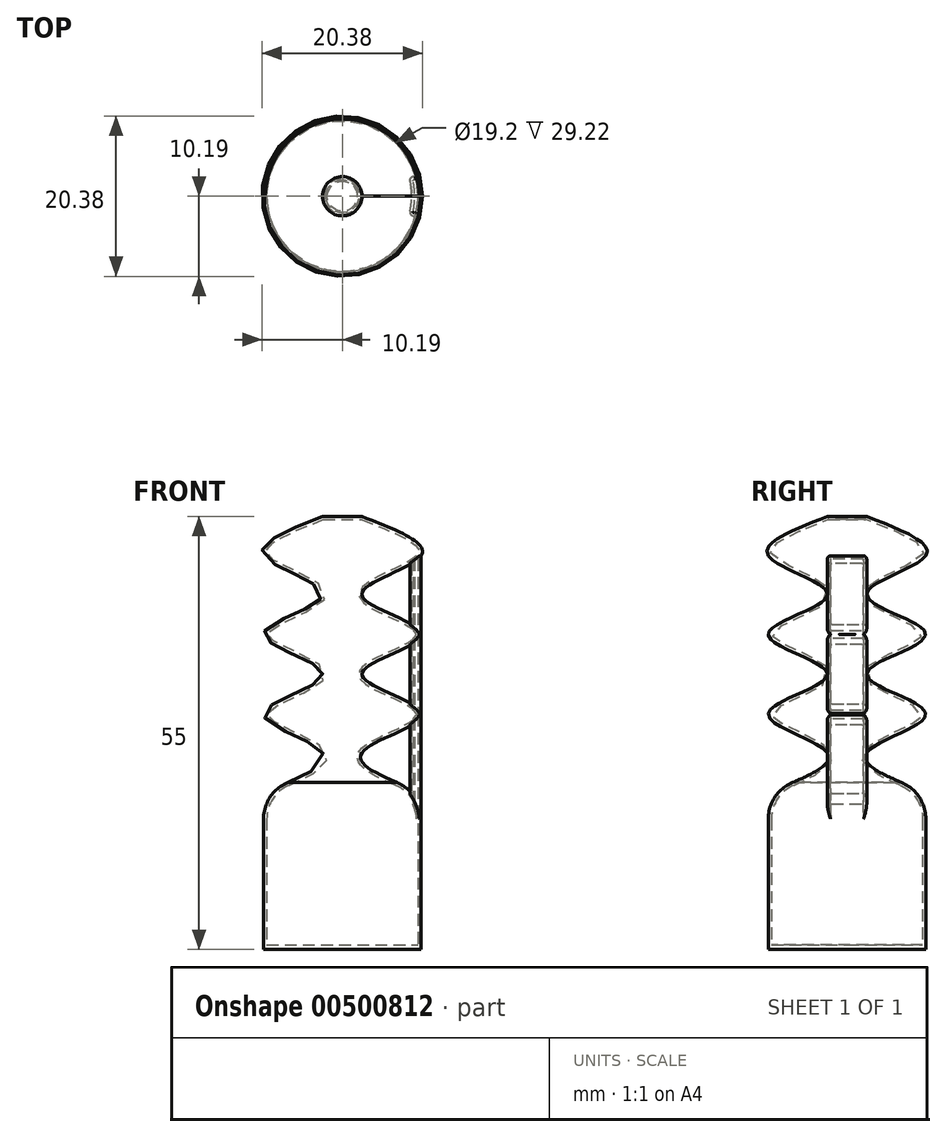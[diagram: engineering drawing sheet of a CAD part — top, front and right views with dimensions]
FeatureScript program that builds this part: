
annotation { "Feature Type Name" : "Feature", "Feature Type Description" : "" }
export const myFeature = defineFeature(function(context is Context, id is Id, definition is map)
    precondition{}
    {
        {
            var Q0;
            Q0=qCreatedBy(makeId("Top.planeOp"),FACE);
            var sketch = newSketch(context, id + "F0", { "sketchPlane" : qUnion([Q0])});
            skCircle(sketch, "E0", {"center": v(0, 0) * mm, "radius": 10 * mm});
            skSolve(sketch);
        }
        {
            var Q0;
            Q0=qSketchRegion(id+"F0",true);
            extrude(context, id + "F1", {"entities" : qUnion([Q0]), "depth" : 20 * mm, "offsetDistance" : 25 * mm});
        }
        {
            var Q0;
            Q0=qCreatedBy(makeId("Top.planeOp"),FACE);
            cPlane(context, id + "F2", {"entities" : qUnion([Q0]), "cplaneType" : CPlaneType.OFFSET, "offset" : 20 * mm, "width" : 150 * mm, "height" : 150 * mm});
        }
        {
            var Q0;
            Q0=qCreatedBy(id+"F2.planeOp",FACE);
            cPlane(context, id + "F3", {"entities" : qUnion([Q0]), "cplaneType" : CPlaneType.OFFSET, "offset" : 5 * mm, "width" : 150 * mm, "height" : 150 * mm});
        }
        {
            var Q0;
            Q0=qCreatedBy(id+"F3.planeOp",FACE);
            cPlane(context, id + "F4", {"entities" : qUnion([Q0]), "cplaneType" : CPlaneType.OFFSET, "offset" : 5 * mm, "width" : 150 * mm, "height" : 150 * mm});
        }
        {
            var Q0;
            Q0=qCreatedBy(id+"F4.planeOp",FACE);
            cPlane(context, id + "F5", {"entities" : qUnion([Q0]), "cplaneType" : CPlaneType.OFFSET, "offset" : 5 * mm, "width" : 150 * mm, "height" : 150 * mm});
        }
        {
            var Q0;
            Q0=qCreatedBy(id+"F5.planeOp",FACE);
            cPlane(context, id + "F6", {"entities" : qUnion([Q0]), "cplaneType" : CPlaneType.OFFSET, "offset" : 5 * mm, "width" : 150 * mm, "height" : 150 * mm});
        }
        {
            var Q0;
            Q0=qCreatedBy(id+"F6.planeOp",FACE);
            cPlane(context, id + "F7", {"entities" : qUnion([Q0]), "cplaneType" : CPlaneType.OFFSET, "offset" : 5 * mm, "width" : 150 * mm, "height" : 150 * mm});
        }
        {
            var Q0;
            Q0=qCreatedBy(id+"F7.planeOp",FACE);
            cPlane(context, id + "F8", {"entities" : qUnion([Q0]), "cplaneType" : CPlaneType.OFFSET, "offset" : 5 * mm, "width" : 150 * mm, "height" : 150 * mm});
        }
        {
            var Q0;
            Q0=qCreatedBy(id+"F8.planeOp",FACE);
            cPlane(context, id + "F9", {"entities" : qUnion([Q0]), "cplaneType" : CPlaneType.OFFSET, "offset" : 5 * mm, "width" : 150 * mm, "height" : 150 * mm});
        }
        {
            var Q0;
            Q0=qCreatedBy(id+"F2.planeOp",FACE);
            var sketch = newSketch(context, id + "F10", { "sketchPlane" : qUnion([Q0])});
            skCircle(sketch, "E1", {"center": v(0, 0) * mm, "radius": 10 * mm});
            skSolve(sketch);
        }
        {
            var Q0;
            Q0=qCreatedBy(id+"F3.planeOp",FACE);
            var sketch = newSketch(context, id + "F11", { "sketchPlane" : qUnion([Q0])});
            skCircle(sketch, "E2", {"center": v(0, 0) * mm, "radius": 2.5 * mm});
            skSolve(sketch);
        }
        {
            var Q0;
            Q0=qCreatedBy(id+"F4.planeOp",FACE);
            var sketch = newSketch(context, id + "F12", { "sketchPlane" : qUnion([Q0])});
            skCircle(sketch, "E3.0", {"center": v(0, 0) * mm, "radius": 10 * mm});
            skSolve(sketch);
        }
        {
            var Q0;
            Q0=qCreatedBy(id+"F5.planeOp",FACE);
            var sketch = newSketch(context, id + "F13", { "sketchPlane" : qUnion([Q0])});
            skCircle(sketch, "E4.0", {"center": v(0, 0) * mm, "radius": 2.5 * mm});
            skSolve(sketch);
        }
        {
            var Q0;
            Q0=qCreatedBy(id+"F6.planeOp",FACE);
            var sketch = newSketch(context, id + "F14", { "sketchPlane" : qUnion([Q0])});
            skCircle(sketch, "E5.0", {"center": v(0, 0) * mm, "radius": 10 * mm});
            skSolve(sketch);
        }
        {
            var Q0;
            Q0=qCreatedBy(id+"F7.planeOp",FACE);
            var sketch = newSketch(context, id + "F15", { "sketchPlane" : qUnion([Q0])});
            skCircle(sketch, "E6.0", {"center": v(0, 0) * mm, "radius": 2.5 * mm});
            skSolve(sketch);
        }
        {
            var Q0;
            Q0=qCreatedBy(id+"F8.planeOp",FACE);
            var sketch = newSketch(context, id + "F16", { "sketchPlane" : qUnion([Q0])});
            skCircle(sketch, "E7.0", {"center": v(0, 0) * mm, "radius": 10 * mm});
            skSolve(sketch);
        }
        {
            var Q0;
            Q0=qCreatedBy(id+"F9.planeOp",FACE);
            var sketch = newSketch(context, id + "F17", { "sketchPlane" : qUnion([Q0])});
            skCircle(sketch, "E8.0", {"center": v(0, 0) * mm, "radius": 2.5 * mm});
            skSolve(sketch);
        }
        {
            var Q1;
            Q1=qSketchRegion(id+"F10",true);
            var Q2;
            Q2=qSketchRegion(id+"F11",true);
            var Q3;
            Q3=qSketchRegion(id+"F12",true);
            var Q4;
            Q4=qSketchRegion(id+"F13",true);
            var Q5;
            Q5=qSketchRegion(id+"F14",true);
            var Q6;
            Q6=qSketchRegion(id+"F15",true);
            var Q7;
            Q7=qSketchRegion(id+"F16",true);
            var Q8;
            Q8=qSketchRegion(id+"F17",true);
            loft(context, id + "F18", {"operationType" : NewBodyOperationType.ADD, "sheetProfilesArray" : [{ "sheetProfileEntities" : qUnion([Q1]) }, { "sheetProfileEntities" : qUnion([Q2]) }, { "sheetProfileEntities" : qUnion([Q3]) }, { "sheetProfileEntities" : qUnion([Q4]) }, { "sheetProfileEntities" : qUnion([Q5]) }, { "sheetProfileEntities" : qUnion([Q6]) }, { "sheetProfileEntities" : qUnion([Q7]) }, { "sheetProfileEntities" : qUnion([Q8]) }]});
        }
        {
            var Q0;
            Q0=makeQuery(id+"F18.boolean.opBoolean","MERGE",EDGE,{"derivedFrom":[makeQuery(id+"F1.opExtrude","CAP_EDGE",EDGE,{"disambiguationData":[OSD([sQuery(id+"F0.wireOp",EDGE,"E0")])],"isStart":false}),makeQuery(id+"F18.opLoft","MID_CAP_EDGE",EDGE,{"disambiguationData":[OSD([sQuery(id+"F10.wireOp",EDGE,"E1")])],"capPos":0.0})]});
            fillet(context, id + "F19", {"entities" : qUnion([Q0]), "radius" : 5 * mm, "tangentPropagation" : true, "allowEdgeOverflow" : false});
        }
        {
            var Q0;
            Q0=makeQuery(id+"F1.opExtrude","CAP_FACE",FACE,{"disambiguationData":[OSD([sQuery(id+"F0.wireOp",EDGE,"E0")])],"isStart":true});
            var sketch = newSketch(context, id + "F20", { "sketchPlane" : qUnion([Q0])});
            skArc(sketch, "E9.0", {"start": v(9.78, -2.1) * mm, "mid": v(10, 0) * mm, "end": v(9.78, 2.1) * mm});
            skLineSegment(sketch, "E10", {"start": v(9.08, 2.5) * mm, "end": v(9.29, 2.5) * mm});
            skArc(sketch, "E11.0", {"start": v(8.6, -1.9) * mm, "mid": v(8.8, 0) * mm, "end": v(8.6, 1.9) * mm});
            skLineSegment(sketch, "E12", {"start": v(9.08, -2.5) * mm, "end": v(9.29, -2.5) * mm});
            skPoint(sketch, "E13.visualSharp", {"position": v(8.44, 2.5) * mm});
            skArc(sketch, "E13.filletArc", {"start": v(9.08, 2.5) * mm, "mid": v(8.7, 2.31) * mm, "end": v(8.6, 1.9) * mm});
            skPoint(sketch, "E14.visualSharp", {"position": v(8.44, -2.5) * mm});
            skArc(sketch, "E14.filletArc", {"start": v(8.6, -1.9) * mm, "mid": v(8.7, -2.31) * mm, "end": v(9.08, -2.5) * mm});
            skPoint(sketch, "E15.visualSharp", {"position": v(9.68, 2.5) * mm});
            skArc(sketch, "E15.filletArc", {"start": v(9.78, 2.1) * mm, "mid": v(9.6, 2.39) * mm, "end": v(9.29, 2.5) * mm});
            skPoint(sketch, "E16.visualSharp", {"position": v(9.68, -2.5) * mm});
            skArc(sketch, "E16.filletArc", {"start": v(9.29, -2.5) * mm, "mid": v(9.6, -2.39) * mm, "end": v(9.78, -2.1) * mm});
            skSolve(sketch);
        }
        {
            var Q0;
            Q0=qSketchRegion(id+"F20",true);
            extrude(context, id + "F21", {"entities" : qUnion([Q0]), "operationType" : NewBodyOperationType.ADD, "oppositeDirection" : true, "depth" : 50 * mm, "offsetDistance" : 25 * mm});
        }
        {
            var Q0;
            Q0=makeQuery(id+"F1.opExtrude","CAP_FACE",FACE,{"disambiguationData":[OSD([sQuery(id+"F0.wireOp",EDGE,"E0")])],"isStart":true});
            shell(context, id + "F22", {"entities" : qUnion([Q0]), "thickness" : .4 * mm});
        }
        {
            var Q0;
            Q0=makeQuery(id+"F1.opExtrude","CAP_FACE",FACE,{"disambiguationData":[OSD([sQuery(id+"F0.wireOp",EDGE,"E0")])],"isStart":true});
            var sketch = newSketch(context, id + "F23", { "sketchPlane" : qUnion([Q0])});
            skCircle(sketch, "E17", {"center": v(0, 0) * mm, "radius": 10 * mm});
            skSolve(sketch);
        }
        {
            var Q0;
            Q0=qSketchRegion(id+"F23",true);
            extrude(context, id + "F24", {"entities" : qUnion([Q0]), "operationType" : NewBodyOperationType.ADD, "oppositeDirection" : true, "depth" : .6 * mm, "offsetDistance" : 25 * mm});
        }
    });
